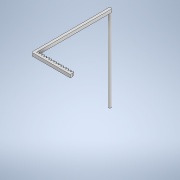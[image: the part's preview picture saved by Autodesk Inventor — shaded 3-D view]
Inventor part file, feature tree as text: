
AUTODESK INVENTOR PART (.ipt)
format: ipt  version: 2021 (Build 250183000, 183)  size: 216,576 bytes
history: native  units: in
note: dims shown in document units (in); Inventor stores cm internally (conversion verified against a paired STEP export)
features: extrude x2, fillet x1, sketch x1
ambient origin geometry x8: Origin, YZ Plane, XZ Plane, XY Plane, X Axis, Y Axis, Z Axis, Center Point
bodies: Solid1 (feature_tree), Solid2 (feature_tree)
feature tree (4):
  extrude  "Extrusion4"  Depth=0.4724in
  extrude  "Extrusion6"  Depth=0.1969in
  fillet  "Fillet3"  [1 undecoded]
  sketch  "Sketch6"  dims[d16=0.3937in d17=0.0in d23=0.4724in d24=11.9685in d25=0.0in d26=0.3937in d27=12.5984in d28=0.0in d29=0.1969in d3=0.0197in d4=1.9685in d5=0.0197in d6=1.9685in d14=0.0197in d15=1.9685in]
note: 1 required parameter value undecoded (feature->parameter linkage not recoverable at this tier; creation-order binding heuristic only, values carry confidence <= 0.55)
